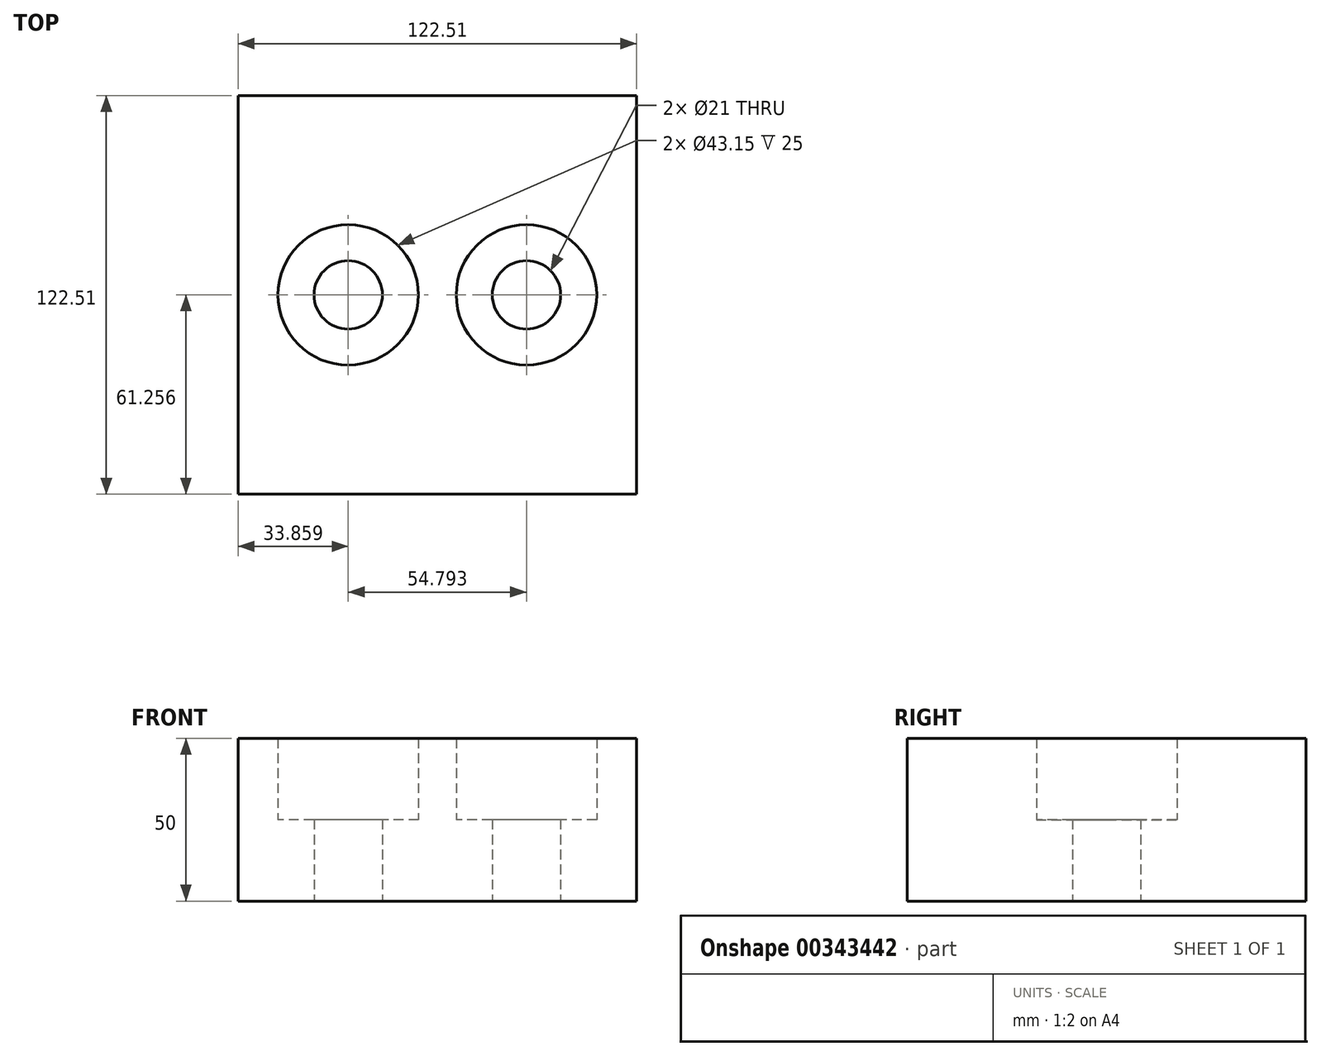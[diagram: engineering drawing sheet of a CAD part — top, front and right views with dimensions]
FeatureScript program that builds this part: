
annotation { "Feature Type Name" : "Feature", "Feature Type Description" : "" }
export const myFeature = defineFeature(function(context is Context, id is Id, definition is map)
    precondition{}
    {
        {
            var Q0;
            Q0=qCreatedBy(makeId("Top.planeOp"),FACE);
            var sketch = newSketch(context, id + "F0", { "sketchPlane" : qUnion([Q0])});
            skLineSegment(sketch, "E0.bottom", {"start": v(0, 0) * mm, "end": v(122.51, 0) * mm});
            skLineSegment(sketch, "E0.top", {"start": v(0, 122.51) * mm, "end": v(122.51, 122.51) * mm});
            skLineSegment(sketch, "E0.left", {"start": v(0, 0) * mm, "end": v(0, 122.51) * mm});
            skLineSegment(sketch, "E0.right", {"start": v(122.51, 0) * mm, "end": v(122.51, 122.51) * mm});
            skCircle(sketch, "E1", {"center": v(33.86, 61.26) * mm, "radius": 10.5 * mm});
            skPoint(sketch, "E1.centerSnap0", {"position": v(0, 61.26) * mm});
            skLineSegment(sketch, "E2", {"start": v(61.26, 171.68) * mm, "end": v(61.26, 224.13) * mm, "construction": true});
            skPoint(sketch, "E2.startSnap0", {"position": v(61.26, 122.51) * mm});
            skCircle(sketch, "E3.MirrorC", {"center": v(88.65, 61.26) * mm, "radius": 10.5 * mm});
            skSolve(sketch);
        }
        {
            var Q0;
            Q0=makeQuery(id+"F0.imprint","IMPRINT",FACE,{"disambiguationData":[TD([[makeQuery(id+"F0.imprint","IMPRINT",EDGE,{"derivedFrom":sQuery(id+"F0.wireOp",EDGE,"E0.bottom")}),1.0]])]});
            extrude(context, id + "F1", {"entities" : qUnion([Q0]), "depth" : 25 * mm});
        }
        {
            var Q0;
            Q0=makeQuery(id+"F1.opExtrude","CAP_FACE",FACE,{"disambiguationData":[OSD([sQuery(id+"F0.wireOp",EDGE,"E0.bottom"),sQuery(id+"F0.wireOp",EDGE,"E0.top"),sQuery(id+"F0.wireOp",EDGE,"E0.left"),sQuery(id+"F0.wireOp",EDGE,"E0.right"),sQuery(id+"F0.wireOp",EDGE,"E1"),sQuery(id+"F0.wireOp",EDGE,"E3.MirrorC")])],"isStart":false});
            var sketch = newSketch(context, id + "F2", { "sketchPlane" : qUnion([Q0])});
            skCircle(sketch, "E4", {"center": v(88.65, 61.26) * mm, "radius": 21.58 * mm});
            skCircle(sketch, "E5.MirrorC", {"center": v(33.86, 61.26) * mm, "radius": 21.58 * mm});
            skSolve(sketch);
        }
        {
            var Q0;
            Q0=makeQuery(id+"F2.imprint","IMPRINT",FACE,{"disambiguationData":[TD([[makeQuery(id+"F2.imprint","IMPRINT",EDGE,{"derivedFrom":sQuery(id+"F2.wireOp",EDGE,"E4")}),-1.0]])]});
            extrude(context, id + "F3", {"entities" : qUnion([Q0]), "operationType" : NewBodyOperationType.ADD, "depth" : 25 * mm});
        }
    });
